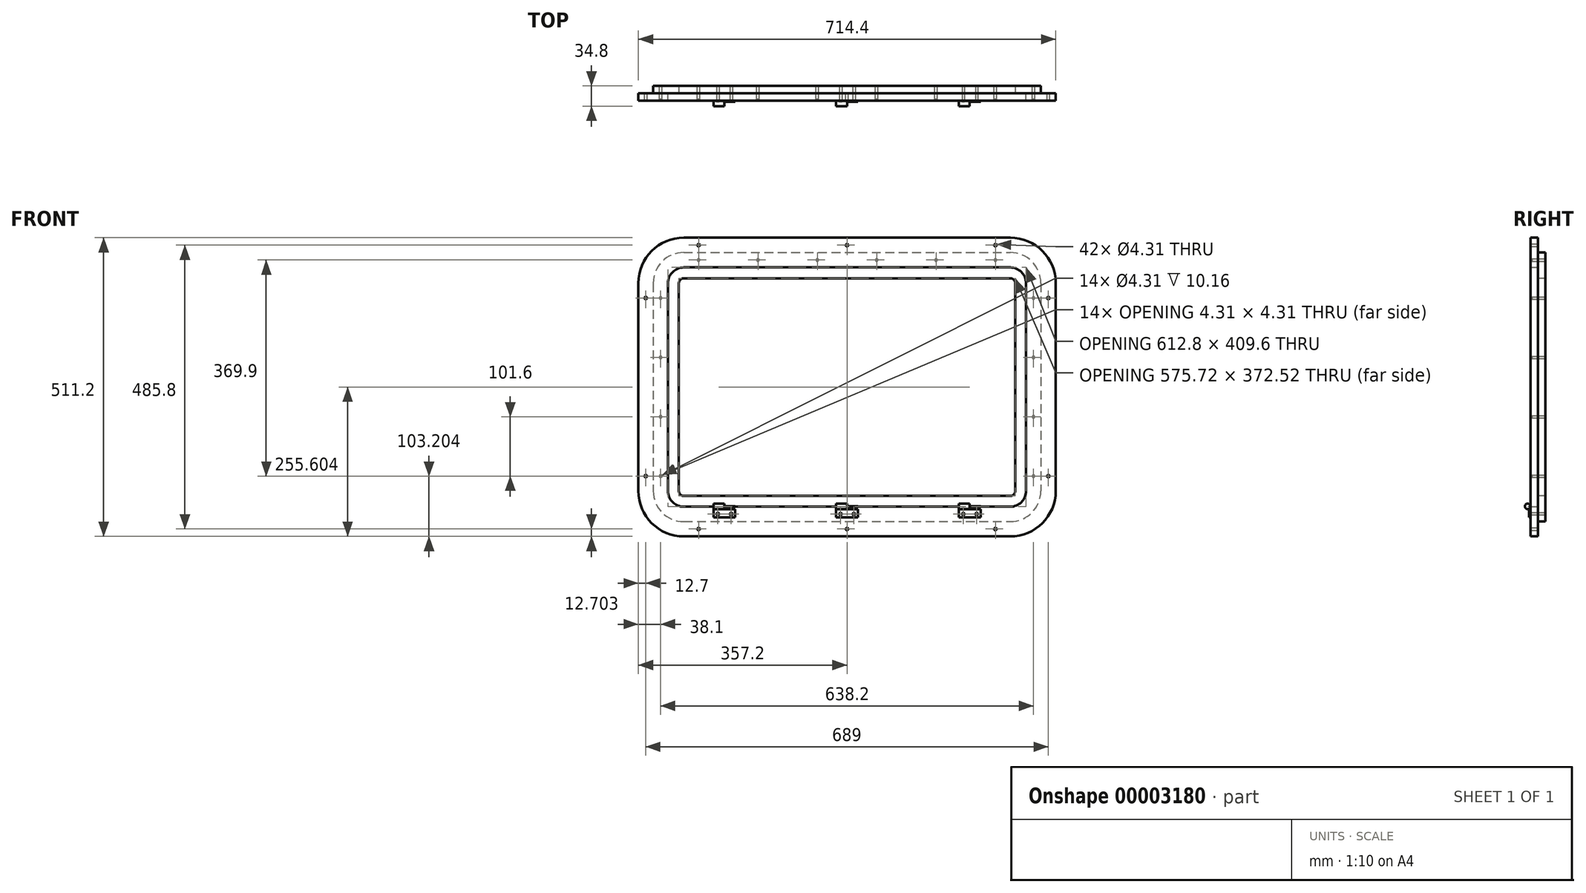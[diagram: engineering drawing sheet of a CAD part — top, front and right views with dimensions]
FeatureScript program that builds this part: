
annotation { "Feature Type Name" : "Feature", "Feature Type Description" : "" }
export const myFeature = defineFeature(function(context is Context, id is Id, definition is map)
    precondition{}
    {
        {
            var Q0;
            Q0=qCreatedBy(makeId("Front.planeOp"),FACE);
            var sketch = newSketch(context, id + "F0", { "sketchPlane" : qUnion([Q0])});
            skLineSegment(sketch, "E0.bottom", {"start": v(-236.07, 236.66) * mm, "end": v(322.73, 236.66) * mm});
            skLineSegment(sketch, "E0.top", {"start": v(-236.07, -169.74) * mm, "end": v(322.73, -169.74) * mm});
            skLineSegment(sketch, "E0.left", {"start": v(-261.47, 211.26) * mm, "end": v(-261.47, -144.34) * mm});
            skLineSegment(sketch, "E0.right", {"start": v(348.13, 211.26) * mm, "end": v(348.13, -144.34) * mm});
            skPoint(sketch, "E1.visualSharp", {"position": v(-261.47, 236.66) * mm});
            skArc(sketch, "E1.filletArc", {"start": v(-236.07, 236.66) * mm, "mid": v(-254.03, 229.22) * mm, "end": v(-261.47, 211.26) * mm});
            skPoint(sketch, "E2.visualSharp", {"position": v(-261.47, -169.74) * mm});
            skArc(sketch, "E2.filletArc", {"start": v(-261.47, -144.34) * mm, "mid": v(-254.03, -162.3) * mm, "end": v(-236.07, -169.74) * mm});
            skPoint(sketch, "E3.visualSharp", {"position": v(348.13, -169.74) * mm});
            skArc(sketch, "E3.filletArc", {"start": v(322.73, -169.74) * mm, "mid": v(340.7, -162.3) * mm, "end": v(348.13, -144.34) * mm});
            skPoint(sketch, "E4.visualSharp", {"position": v(348.13, 236.66) * mm});
            skArc(sketch, "E4.filletArc", {"start": v(348.13, 211.26) * mm, "mid": v(340.7, 229.22) * mm, "end": v(322.73, 236.66) * mm});
            skArc(sketch, "E5.0", {"start": v(-236.07, 238.26) * mm, "mid": v(-255.16, 230.36) * mm, "end": v(-263.07, 211.26) * mm});
            skLineSegment(sketch, "E5.1", {"start": v(-236.07, 238.26) * mm, "end": v(322.73, 238.26) * mm});
            skArc(sketch, "E5.2", {"start": v(349.73, 211.26) * mm, "mid": v(341.82, 230.36) * mm, "end": v(322.73, 238.26) * mm});
            skLineSegment(sketch, "E5.3", {"start": v(349.73, 211.26) * mm, "end": v(349.73, -144.34) * mm});
            skArc(sketch, "E5.4", {"start": v(322.73, -171.34) * mm, "mid": v(341.82, -163.43) * mm, "end": v(349.73, -144.34) * mm});
            skLineSegment(sketch, "E5.5", {"start": v(-263.07, 211.26) * mm, "end": v(-263.07, -144.34) * mm});
            skLineSegment(sketch, "E5.6", {"start": v(-236.07, -171.34) * mm, "end": v(322.73, -171.34) * mm});
            skArc(sketch, "E5.7", {"start": v(-263.07, -144.34) * mm, "mid": v(-255.16, -163.43) * mm, "end": v(-236.07, -171.34) * mm});
            skArc(sketch, "E6.0", {"start": v(-236.07, 219.72) * mm, "mid": v(-242.05, 217.24) * mm, "end": v(-244.53, 211.26) * mm});
            skLineSegment(sketch, "E6.1", {"start": v(-236.07, 219.72) * mm, "end": v(322.73, 219.72) * mm});
            skArc(sketch, "E6.2", {"start": v(331.19, 211.26) * mm, "mid": v(328.71, 217.24) * mm, "end": v(322.73, 219.72) * mm});
            skLineSegment(sketch, "E6.3", {"start": v(331.19, 211.26) * mm, "end": v(331.19, -144.34) * mm});
            skArc(sketch, "E6.4", {"start": v(322.73, -152.8) * mm, "mid": v(328.71, -150.32) * mm, "end": v(331.19, -144.34) * mm});
            skLineSegment(sketch, "E6.5", {"start": v(-244.53, 211.26) * mm, "end": v(-244.53, -144.34) * mm});
            skLineSegment(sketch, "E6.6", {"start": v(-236.07, -152.8) * mm, "end": v(322.73, -152.8) * mm});
            skArc(sketch, "E6.7", {"start": v(-244.53, -144.34) * mm, "mid": v(-242.05, -150.32) * mm, "end": v(-236.07, -152.8) * mm});
            skArc(sketch, "E7.0", {"start": v(-236.07, 289.06) * mm, "mid": v(-291.08, 266.28) * mm, "end": v(-313.87, 211.26) * mm});
            skLineSegment(sketch, "E7.1", {"start": v(-236.07, 289.06) * mm, "end": v(322.73, 289.06) * mm});
            skArc(sketch, "E7.2", {"start": v(400.53, 211.26) * mm, "mid": v(377.74, 266.28) * mm, "end": v(322.73, 289.06) * mm});
            skLineSegment(sketch, "E7.3", {"start": v(400.53, 211.26) * mm, "end": v(400.53, -144.34) * mm});
            skArc(sketch, "E7.4", {"start": v(322.73, -222.14) * mm, "mid": v(377.74, -199.35) * mm, "end": v(400.53, -144.34) * mm});
            skLineSegment(sketch, "E7.5", {"start": v(-313.87, 211.26) * mm, "end": v(-313.87, -144.34) * mm});
            skLineSegment(sketch, "E7.6", {"start": v(-236.07, -222.14) * mm, "end": v(322.73, -222.14) * mm});
            skArc(sketch, "E7.7", {"start": v(-313.87, -144.34) * mm, "mid": v(-291.08, -199.35) * mm, "end": v(-236.07, -222.14) * mm});
            skArc(sketch, "E8.0", {"start": v(-236.07, 263.66) * mm, "mid": v(-273.12, 248.32) * mm, "end": v(-288.47, 211.26) * mm});
            skLineSegment(sketch, "E8.1", {"start": v(-236.07, 263.66) * mm, "end": v(322.73, 263.66) * mm});
            skArc(sketch, "E8.2", {"start": v(375.13, 211.26) * mm, "mid": v(359.78, 248.32) * mm, "end": v(322.73, 263.66) * mm});
            skLineSegment(sketch, "E8.3", {"start": v(375.13, 211.26) * mm, "end": v(375.13, -144.34) * mm});
            skArc(sketch, "E8.4", {"start": v(322.73, -196.74) * mm, "mid": v(359.78, -181.39) * mm, "end": v(375.13, -144.34) * mm});
            skLineSegment(sketch, "E8.5", {"start": v(-288.47, 211.26) * mm, "end": v(-288.47, -144.34) * mm});
            skLineSegment(sketch, "E8.6", {"start": v(-236.07, -196.74) * mm, "end": v(322.73, -196.74) * mm});
            skArc(sketch, "E8.7", {"start": v(-288.47, -144.34) * mm, "mid": v(-273.12, -181.39) * mm, "end": v(-236.07, -196.74) * mm});
            skSolve(sketch);
        }
        {
            var Q0;
            Q0=makeQuery(id+"F0.imprint","IMPRINT",FACE,{"disambiguationData":[TD([[makeQuery(id+"F0.imprint","IMPRINT",EDGE,{"derivedFrom":sQuery(id+"F0.wireOp",EDGE,"E5.0")}),-1.0]])]});
            var Q1;
            Q1=makeQuery(id+"F0.imprint","IMPRINT",FACE,{"disambiguationData":[TD([[makeQuery(id+"F0.imprint","IMPRINT",EDGE,{"derivedFrom":sQuery(id+"F0.wireOp",EDGE,"E0.bottom")}),1.0]])]});
            var Q2;
            Q2=makeQuery(id+"F0.imprint","IMPRINT",FACE,{"disambiguationData":[TD([[makeQuery(id+"F0.imprint","IMPRINT",EDGE,{"derivedFrom":sQuery(id+"F0.wireOp",EDGE,"E0.bottom")}),-1.0]])]});
            extrude(context, id + "F1", {"entities" : qUnion([Q0, Q1, Q2]), "oppositeDirection" : true, "depth" : 12.7 * mm});
        }
        {
            var Q0;
            Q0=makeQuery(id+"F0.imprint","IMPRINT",FACE,{"disambiguationData":[TD([[makeQuery(id+"F0.imprint","IMPRINT",EDGE,{"derivedFrom":sQuery(id+"F0.wireOp",EDGE,"E7.0")}),1.0]])]});
            var Q1;
            Q1=makeQuery(id+"F0.imprint","IMPRINT",FACE,{"disambiguationData":[TD([[makeQuery(id+"F0.imprint","IMPRINT",EDGE,{"derivedFrom":sQuery(id+"F0.wireOp",EDGE,"E5.0")}),-1.0]])]});
            extrude(context, id + "F2", {"entities" : qUnion([Q0, Q1]), "depth" : 12.7 * mm});
        }
        {
            var Q0;
            Q0=makeQuery(id+"F2.opExtrude","CAP_FACE",FACE,{"disambiguationData":[OSD([sQuery(id+"F0.wireOp",EDGE,"E5.0"),sQuery(id+"F0.wireOp",EDGE,"E5.1"),sQuery(id+"F0.wireOp",EDGE,"E5.2"),sQuery(id+"F0.wireOp",EDGE,"E5.3"),sQuery(id+"F0.wireOp",EDGE,"E5.4"),sQuery(id+"F0.wireOp",EDGE,"E5.5"),sQuery(id+"F0.wireOp",EDGE,"E5.6"),sQuery(id+"F0.wireOp",EDGE,"E5.7"),sQuery(id+"F0.wireOp",EDGE,"E7.0"),sQuery(id+"F0.wireOp",EDGE,"E7.1"),sQuery(id+"F0.wireOp",EDGE,"E7.2"),sQuery(id+"F0.wireOp",EDGE,"E7.3"),sQuery(id+"F0.wireOp",EDGE,"E7.4"),sQuery(id+"F0.wireOp",EDGE,"E7.5"),sQuery(id+"F0.wireOp",EDGE,"E7.6"),sQuery(id+"F0.wireOp",EDGE,"E7.7")])],"isStart":false});
            var sketch = newSketch(context, id + "F3", { "sketchPlane" : qUnion([Q0])});
            skLineSegment(sketch, "E9.0", {"start": v(-261.47, 211.26) * mm, "end": v(-261.47, -144.34) * mm});
            skLineSegment(sketch, "E9.1", {"start": v(-236.07, -169.74) * mm, "end": v(322.73, -169.74) * mm});
            skLineSegment(sketch, "E10.bottom", {"start": v(-185.27, -189.6) * mm, "end": v(-148.19, -189.6) * mm});
            skLineSegment(sketch, "E10.top", {"start": v(-185.27, -170.55) * mm, "end": v(-148.19, -170.55) * mm});
            skLineSegment(sketch, "E10.left", {"start": v(-185.27, -189.6) * mm, "end": v(-185.27, -170.55) * mm});
            skLineSegment(sketch, "E10.right", {"start": v(-148.19, -189.6) * mm, "end": v(-148.19, -170.55) * mm});
            skLineSegment(sketch, "E11.bottom", {"start": v(-166.85, -170.55) * mm, "end": v(-148.19, -170.55) * mm});
            skLineSegment(sketch, "E11.top", {"start": v(-166.85, -175.32) * mm, "end": v(-148.19, -175.32) * mm});
            skLineSegment(sketch, "E11.left", {"start": v(-166.85, -170.55) * mm, "end": v(-166.85, -175.32) * mm});
            skLineSegment(sketch, "E11.right", {"start": v(-148.19, -170.55) * mm, "end": v(-148.19, -175.32) * mm});
            skCircle(sketch, "E12", {"center": v(-177.78, -183.76) * mm, "radius": 2.15 * mm});
            skCircle(sketch, "E13", {"center": v(-154.92, -183.76) * mm, "radius": 2.15 * mm});
            skSolve(sketch);
        }
        {
            var Q0;
            {var subQ6=sQuery(id+"F3.wireOp",EDGE,"E10.bottom");Q0=makeQuery(id+"F3.imprint","IMPRINT",FACE,{"disambiguationData":[TD([[makeQuery(id+"F3.imprint","IMPRINT",EDGE,{"derivedFrom":subQ6}),1.0]])]});}
            var Q1;
            {var subQ5=sQuery(id+"F3.wireOp",EDGE,"E10.top");Q1=makeQuery(id+"F3.imprint","IMPRINT",FACE,{"disambiguationData":[TD([[makeQuery(id+"F3.imprint","IMPRINT",EDGE,{"derivedFrom":subQ5}),-1.0]])]});}
            var Q2;
            {var subQ3=sQuery(id+"F3.wireOp",EDGE,"E10.left");var subQ5=sQuery(id+"F3.wireOp",EDGE,"E9.1");var subQ7=makeQuery(id+"F3.imprint","INTERSECT",VERTEX,{"derivedFrom":[subQ5,subQ3]});Q2=makeQuery(id+"F3.imprint","IMPRINT",FACE,{"disambiguationData":[TD([[makeQuery(id+"F3.imprint","IMPRINT",EDGE,{"disambiguationData":[TD([[subQ7,-1.0]])],"derivedFrom":subQ5}),-1.0]])]});}
            extrude(context, id + "F4", {"entities" : qUnion([Q0, Q1, Q2]), "depth" : 2.03 * mm});
        }
        {
            var Q0;
            Q0=makeQuery(id+"F4.opExtrude","SWEPT_FACE",FACE,{"disambiguationData":[OSD([sQuery(id+"F3.wireOp",EDGE,"E10.left")])]});
            var sketch = newSketch(context, id + "F5", { "sketchPlane" : qUnion([Q0])});
            skCircle(sketch, "E14", {"center": v(17.4, -170.55) * mm, "radius": 4.7 * mm});
            skSolve(sketch);
        }
        {
            var Q0;
            {var subQ0=sQuery(id+"F3.wireOp",EDGE,"E10.left");var subQ4=makeQuery(id+"F4.opExtrude","SWEPT_EDGE",EDGE,{"disambiguationData":[OSD([sQuery(id+"F3.wireOp",EDGE,"E10.top"),subQ0])]});Q0=makeQuery(id+"F5.imprint","IMPRINT",FACE,{"disambiguationData":[TD([[makeQuery(id+"F5.imprint","IMPRINT",EDGE,{"derivedFrom":subQ4}),-1.0]])]});}
            var Q1;
            {var subQ0=sQuery(id+"F3.wireOp",EDGE,"E10.left");var subQ4=makeQuery(id+"F4.opExtrude","SWEPT_EDGE",EDGE,{"disambiguationData":[OSD([sQuery(id+"F3.wireOp",EDGE,"E10.top"),subQ0])]});Q1=makeQuery(id+"F5.imprint","IMPRINT",FACE,{"disambiguationData":[TD([[makeQuery(id+"F5.imprint","IMPRINT",EDGE,{"derivedFrom":subQ4}),1.0]])]});}
            extrude(context, id + "F6", {"entities" : qUnion([Q0, Q1]), "operationType" : NewBodyOperationType.ADD, "oppositeDirection" : true, "depth" : 18.54 * mm});
        }
        {
            var Q0;
            Q0=makeQuery(id+"F4.opExtrude","SWEPT_BODY",BODY,{"disambiguationData":[OSD([sQuery(id+"F3.wireOp",EDGE,"E10.bottom"),sQuery(id+"F3.wireOp",EDGE,"E10.top"),sQuery(id+"F3.wireOp",EDGE,"E10.left"),sQuery(id+"F3.wireOp",EDGE,"E10.right"),sQuery(id+"F3.wireOp",EDGE,"E11.top"),sQuery(id+"F3.wireOp",EDGE,"E11.left"),sQuery(id+"F3.wireOp",EDGE,"E12"),sQuery(id+"F3.wireOp",EDGE,"E13")])]});
            var Q1;
            Q1=sQuery(id+"F3.wireOp",EDGE,"E9.0");
            var Q2;
            Q2=sQuery(id+"F3.wireOp",EDGE,"E9.1");
            transform(context, id + "F7", {"entities" : qUnion([Q0]), "transformType" : TransformType.TRANSLATION_3D, "dx" : 210.06 * mm, "dy" : 0 * mm, "dz" : 0 * mm, "makeCopy" : true});
        }
        {
            var Q0;
            Q0=makeQuery(id+"F4.opExtrude","SWEPT_BODY",BODY,{"disambiguationData":[OSD([sQuery(id+"F3.wireOp",EDGE,"E10.bottom"),sQuery(id+"F3.wireOp",EDGE,"E10.top"),sQuery(id+"F3.wireOp",EDGE,"E10.left"),sQuery(id+"F3.wireOp",EDGE,"E10.right"),sQuery(id+"F3.wireOp",EDGE,"E11.top"),sQuery(id+"F3.wireOp",EDGE,"E11.left"),sQuery(id+"F3.wireOp",EDGE,"E12"),sQuery(id+"F3.wireOp",EDGE,"E13")])]});
            var Q1;
            Q1=sQuery(id+"F3.wireOp",EDGE,"E9.1");
            transform(context, id + "F8", {"entities" : qUnion([Q0]), "transformType" : TransformType.TRANSLATION_3D, "dx" : 420.12 * mm, "dy" : 0 * mm, "dz" : 0 * mm, "makeCopy" : true});
        }
        {
            var Q0;
            {var subQ8=sQuery(id+"F3.wireOp",EDGE,"E10.bottom");Q0=makeQuery(id+"F3.imprint","IMPRINT",FACE,{"disambiguationData":[TD([[makeQuery(id+"F3.imprint","IMPRINT",EDGE,{"derivedFrom":subQ8}),-1.0]])]});}
            var sketch = newSketch(context, id + "F9", { "sketchPlane" : qUnion([Q0])});
            skCircle(sketch, "E15.0", {"center": v(-177.78, -183.76) * mm, "radius": 2.15 * mm});
            skCircle(sketch, "E15.1", {"center": v(-154.92, -183.76) * mm, "radius": 2.15 * mm});
            skCircle(sketch, "E15.2", {"center": v(32.28, -183.76) * mm, "radius": 2.15 * mm});
            skCircle(sketch, "E15.3", {"center": v(55.14, -183.76) * mm, "radius": 2.15 * mm});
            skCircle(sketch, "E15.4", {"center": v(242.34, -183.76) * mm, "radius": 2.15 * mm});
            skCircle(sketch, "E15.5", {"center": v(265.2, -183.76) * mm, "radius": 2.15 * mm});
            skSolve(sketch);
        }
        {
            var Q0;
            Q0=makeQuery(id+"F9.imprint","IMPRINT",FACE,{"disambiguationData":[TD([[makeQuery(id+"F9.imprint","IMPRINT",EDGE,{"derivedFrom":sQuery(id+"F9.wireOp",EDGE,"E15.0")}),1.0]])]});
            var Q1;
            Q1=makeQuery(id+"F9.imprint","IMPRINT",FACE,{"disambiguationData":[TD([[makeQuery(id+"F9.imprint","IMPRINT",EDGE,{"derivedFrom":sQuery(id+"F9.wireOp",EDGE,"E15.1")}),1.0]])]});
            var Q2;
            Q2=makeQuery(id+"F9.imprint","IMPRINT",FACE,{"disambiguationData":[TD([[makeQuery(id+"F9.imprint","IMPRINT",EDGE,{"derivedFrom":sQuery(id+"F9.wireOp",EDGE,"E15.2")}),1.0]])]});
            var Q3;
            Q3=makeQuery(id+"F9.imprint","IMPRINT",FACE,{"disambiguationData":[TD([[makeQuery(id+"F9.imprint","IMPRINT",EDGE,{"derivedFrom":sQuery(id+"F9.wireOp",EDGE,"E15.3")}),1.0]])]});
            var Q4;
            Q4=makeQuery(id+"F9.imprint","IMPRINT",FACE,{"disambiguationData":[TD([[makeQuery(id+"F9.imprint","IMPRINT",EDGE,{"derivedFrom":sQuery(id+"F9.wireOp",EDGE,"E15.4")}),1.0]])]});
            var Q5;
            Q5=makeQuery(id+"F9.imprint","IMPRINT",FACE,{"disambiguationData":[TD([[makeQuery(id+"F9.imprint","IMPRINT",EDGE,{"derivedFrom":sQuery(id+"F9.wireOp",EDGE,"E15.5")}),1.0]])]});
            extrude(context, id + "F10", {"entities" : qUnion([Q0, Q1, Q2, Q3, Q4, Q5]), "operationType" : NewBodyOperationType.REMOVE, "oppositeDirection" : true, "depth" : 25.4 * mm});
        }
        {
            var Q0;
            Q0=makeQuery(id+"F1.opExtrude","CAP_FACE",FACE,{"disambiguationData":[OSD([sQuery(id+"F0.wireOp",EDGE,"E6.0"),sQuery(id+"F0.wireOp",EDGE,"E6.1"),sQuery(id+"F0.wireOp",EDGE,"E6.2"),sQuery(id+"F0.wireOp",EDGE,"E6.3"),sQuery(id+"F0.wireOp",EDGE,"E6.4"),sQuery(id+"F0.wireOp",EDGE,"E6.5"),sQuery(id+"F0.wireOp",EDGE,"E6.6"),sQuery(id+"F0.wireOp",EDGE,"E6.7"),sQuery(id+"F0.wireOp",EDGE,"E8.0"),sQuery(id+"F0.wireOp",EDGE,"E8.1"),sQuery(id+"F0.wireOp",EDGE,"E8.2"),sQuery(id+"F0.wireOp",EDGE,"E8.3"),sQuery(id+"F0.wireOp",EDGE,"E8.4"),sQuery(id+"F0.wireOp",EDGE,"E8.5"),sQuery(id+"F0.wireOp",EDGE,"E8.6"),sQuery(id+"F0.wireOp",EDGE,"E8.7")])],"isStart":false});
            var sketch = newSketch(context, id + "F11", { "sketchPlane" : qUnion([Q0])});
            skCircle(sketch, "E16", {"center": v(-297.33, 250.96) * mm, "radius": 2.15 * mm});
            skCircle(sketch, "E17.1.0.0", {"center": v(-195.73, 250.96) * mm, "radius": 2.15 * mm});
            skCircle(sketch, "E17.2.0.0", {"center": v(-94.13, 250.96) * mm, "radius": 2.15 * mm});
            skLineSegment(sketch, "E17.direction1", {"start": v(-297.33, 250.96) * mm, "end": v(-195.73, 250.96) * mm, "construction": true});
            skCircle(sketch, "E18.0.3.0", {"center": v(7.47, 250.96) * mm, "radius": 2.15 * mm});
            skCircle(sketch, "E18.0.4.0", {"center": v(109.07, 250.96) * mm, "radius": 2.15 * mm});
            skCircle(sketch, "E19.0.5.0", {"center": v(210.67, 250.96) * mm, "radius": 2.15 * mm});
            skCircle(sketch, "E20", {"center": v(-362.43, 185.86) * mm, "radius": 2.15 * mm});
            skCircle(sketch, "E21.0.1.0", {"center": v(-362.43, 84.26) * mm, "radius": 2.15 * mm});
            skCircle(sketch, "E21.0.2.0", {"center": v(-362.43, -17.34) * mm, "radius": 2.15 * mm});
            skCircle(sketch, "E21.0.3.0", {"center": v(-362.43, -118.94) * mm, "radius": 2.15 * mm});
            skLineSegment(sketch, "E21.direction1", {"start": v(-362.43, 185.86) * mm, "end": v(-337.03, 185.86) * mm, "construction": true});
            skLineSegment(sketch, "E21.direction2", {"start": v(-362.43, 185.86) * mm, "end": v(-362.43, 84.26) * mm, "construction": true});
            skLineSegment(sketch, "E22.0", {"start": v(288.47, 211.26) * mm, "end": v(288.47, -144.34) * mm});
            skCircle(sketch, "E23", {"center": v(275.77, 185.86) * mm, "radius": 2.15 * mm});
            skCircle(sketch, "E24.0.1.0", {"center": v(275.77, 84.26) * mm, "radius": 2.15 * mm});
            skCircle(sketch, "E24.0.2.0", {"center": v(275.77, -17.34) * mm, "radius": 2.15 * mm});
            skCircle(sketch, "E24.0.3.0", {"center": v(275.77, -118.94) * mm, "radius": 2.15 * mm});
            skLineSegment(sketch, "E24.direction1", {"start": v(275.77, 185.86) * mm, "end": v(301.17, 185.86) * mm, "construction": true});
            skLineSegment(sketch, "E24.direction2", {"start": v(275.77, 185.86) * mm, "end": v(275.77, 84.26) * mm, "construction": true});
            skSolve(sketch);
        }
        {
            var Q0;
            Q0=makeQuery(id+"F11.imprint","IMPRINT",FACE,{"disambiguationData":[TD([[makeQuery(id+"F11.imprint","IMPRINT",EDGE,{"derivedFrom":sQuery(id+"F11.wireOp",EDGE,"E21.0.3.0")}),1.0]])]});
            var Q1;
            Q1=makeQuery(id+"F11.imprint","IMPRINT",FACE,{"disambiguationData":[TD([[makeQuery(id+"F11.imprint","IMPRINT",EDGE,{"derivedFrom":sQuery(id+"F11.wireOp",EDGE,"E21.0.2.0")}),1.0]])]});
            var Q2;
            Q2=makeQuery(id+"F11.imprint","IMPRINT",FACE,{"disambiguationData":[TD([[makeQuery(id+"F11.imprint","IMPRINT",EDGE,{"derivedFrom":sQuery(id+"F11.wireOp",EDGE,"E21.0.1.0")}),1.0]])]});
            var Q3;
            Q3=makeQuery(id+"F11.imprint","IMPRINT",FACE,{"disambiguationData":[TD([[makeQuery(id+"F11.imprint","IMPRINT",EDGE,{"derivedFrom":sQuery(id+"F11.wireOp",EDGE,"E20")}),1.0]])]});
            var Q4;
            Q4=makeQuery(id+"F11.imprint","IMPRINT",FACE,{"disambiguationData":[TD([[makeQuery(id+"F11.imprint","IMPRINT",EDGE,{"derivedFrom":sQuery(id+"F11.wireOp",EDGE,"E16")}),1.0]])]});
            var Q5;
            Q5=makeQuery(id+"F11.imprint","IMPRINT",FACE,{"disambiguationData":[TD([[makeQuery(id+"F11.imprint","IMPRINT",EDGE,{"derivedFrom":sQuery(id+"F11.wireOp",EDGE,"E17.1.0.0")}),1.0]])]});
            var Q6;
            Q6=makeQuery(id+"F11.imprint","IMPRINT",FACE,{"disambiguationData":[TD([[makeQuery(id+"F11.imprint","IMPRINT",EDGE,{"derivedFrom":sQuery(id+"F11.wireOp",EDGE,"E17.2.0.0")}),1.0]])]});
            var Q7;
            Q7=makeQuery(id+"F11.imprint","IMPRINT",FACE,{"disambiguationData":[TD([[makeQuery(id+"F11.imprint","IMPRINT",EDGE,{"derivedFrom":sQuery(id+"F11.wireOp",EDGE,"E18.0.3.0")}),1.0]])]});
            var Q8;
            Q8=makeQuery(id+"F11.imprint","IMPRINT",FACE,{"disambiguationData":[TD([[makeQuery(id+"F11.imprint","IMPRINT",EDGE,{"derivedFrom":sQuery(id+"F11.wireOp",EDGE,"E18.0.4.0")}),1.0]])]});
            var Q9;
            Q9=makeQuery(id+"F11.imprint","IMPRINT",FACE,{"disambiguationData":[TD([[makeQuery(id+"F11.imprint","IMPRINT",EDGE,{"derivedFrom":sQuery(id+"F11.wireOp",EDGE,"E19.0.5.0")}),1.0]])]});
            var Q10;
            Q10=makeQuery(id+"F11.imprint","IMPRINT",FACE,{"disambiguationData":[TD([[makeQuery(id+"F11.imprint","IMPRINT",EDGE,{"derivedFrom":sQuery(id+"F11.wireOp",EDGE,"E23")}),1.0]])]});
            var Q11;
            Q11=makeQuery(id+"F11.imprint","IMPRINT",FACE,{"disambiguationData":[TD([[makeQuery(id+"F11.imprint","IMPRINT",EDGE,{"derivedFrom":sQuery(id+"F11.wireOp",EDGE,"E24.0.1.0")}),1.0]])]});
            var Q12;
            Q12=makeQuery(id+"F11.imprint","IMPRINT",FACE,{"disambiguationData":[TD([[makeQuery(id+"F11.imprint","IMPRINT",EDGE,{"derivedFrom":sQuery(id+"F11.wireOp",EDGE,"E24.0.2.0")}),1.0]])]});
            var Q13;
            Q13=makeQuery(id+"F11.imprint","IMPRINT",FACE,{"disambiguationData":[TD([[makeQuery(id+"F11.imprint","IMPRINT",EDGE,{"derivedFrom":sQuery(id+"F11.wireOp",EDGE,"E24.0.3.0")}),1.0]])]});
            extrude(context, id + "F12", {"entities" : qUnion([Q0, Q1, Q2, Q3, Q4, Q5, Q6, Q7, Q8, Q9, Q10, Q11, Q12, Q13]), "operationType" : NewBodyOperationType.REMOVE, "oppositeDirection" : true, "depth" : 22.86 * mm});
        }
        {
            var Q0;
            Q0=makeQuery(id+"F0.imprint","IMPRINT",FACE,{"disambiguationData":[TD([[makeQuery(id+"F0.imprint","IMPRINT",EDGE,{"derivedFrom":sQuery(id+"F0.wireOp",EDGE,"E7.0")}),1.0]])]});
            var sketch = newSketch(context, id + "F13", { "sketchPlane" : qUnion([Q0])});
            skCircle(sketch, "E25", {"center": v(362.43, 185.86) * mm, "radius": 1.38 * mm});
            skCircle(sketch, "E26", {"center": v(297.33, 250.96) * mm, "radius": 1.38 * mm});
            skCircle(sketch, "E27", {"center": v(195.73, 250.96) * mm, "radius": 1.38 * mm});
            skCircle(sketch, "E28", {"center": v(94.13, 250.96) * mm, "radius": 1.38 * mm});
            skCircle(sketch, "E29", {"center": v(-7.47, 250.96) * mm, "radius": 1.38 * mm});
            skCircle(sketch, "E30", {"center": v(362.43, 84.26) * mm, "radius": 1.38 * mm});
            skCircle(sketch, "E31", {"center": v(362.43, -17.34) * mm, "radius": 1.38 * mm});
            skCircle(sketch, "E32", {"center": v(362.43, -118.94) * mm, "radius": 1.38 * mm});
            skCircle(sketch, "E33", {"center": v(-109.07, 250.96) * mm, "radius": 1.38 * mm});
            skCircle(sketch, "E34", {"center": v(-210.67, 250.96) * mm, "radius": 1.38 * mm});
            skCircle(sketch, "E35", {"center": v(-275.77, 185.86) * mm, "radius": 1.38 * mm});
            skCircle(sketch, "E36", {"center": v(-275.77, 84.26) * mm, "radius": 1.38 * mm});
            skCircle(sketch, "E37", {"center": v(-275.77, -17.34) * mm, "radius": 1.38 * mm});
            skCircle(sketch, "E38", {"center": v(-275.77, -118.94) * mm, "radius": 1.38 * mm});
            skSolve(sketch);
        }
        {
            var Q0;
            Q0=makeQuery(id+"F13.imprint","IMPRINT",FACE,{"disambiguationData":[TD([[makeQuery(id+"F13.imprint","IMPRINT",EDGE,{"derivedFrom":sQuery(id+"F13.wireOp",EDGE,"E29")}),1.0]])]});
            var Q1;
            Q1=makeQuery(id+"F13.imprint","IMPRINT",FACE,{"disambiguationData":[TD([[makeQuery(id+"F13.imprint","IMPRINT",EDGE,{"derivedFrom":sQuery(id+"F13.wireOp",EDGE,"E36")}),1.0]])]});
            var Q2;
            Q2=makeQuery(id+"F13.imprint","IMPRINT",FACE,{"disambiguationData":[TD([[makeQuery(id+"F13.imprint","IMPRINT",EDGE,{"derivedFrom":sQuery(id+"F13.wireOp",EDGE,"E32")}),1.0]])]});
            var Q3;
            Q3=makeQuery(id+"F13.imprint","IMPRINT",FACE,{"disambiguationData":[TD([[makeQuery(id+"F13.imprint","IMPRINT",EDGE,{"derivedFrom":sQuery(id+"F13.wireOp",EDGE,"E33")}),1.0]])]});
            var Q4;
            Q4=makeQuery(id+"F13.imprint","IMPRINT",FACE,{"disambiguationData":[TD([[makeQuery(id+"F13.imprint","IMPRINT",EDGE,{"derivedFrom":sQuery(id+"F13.wireOp",EDGE,"E37")}),1.0]])]});
            var Q5;
            Q5=makeQuery(id+"F13.imprint","IMPRINT",FACE,{"disambiguationData":[TD([[makeQuery(id+"F13.imprint","IMPRINT",EDGE,{"derivedFrom":sQuery(id+"F13.wireOp",EDGE,"E26")}),1.0]])]});
            var Q6;
            Q6=makeQuery(id+"F13.imprint","IMPRINT",FACE,{"disambiguationData":[TD([[makeQuery(id+"F13.imprint","IMPRINT",EDGE,{"derivedFrom":sQuery(id+"F13.wireOp",EDGE,"E25")}),1.0]])]});
            var Q7;
            Q7=makeQuery(id+"F13.imprint","IMPRINT",FACE,{"disambiguationData":[TD([[makeQuery(id+"F13.imprint","IMPRINT",EDGE,{"derivedFrom":sQuery(id+"F13.wireOp",EDGE,"E35")}),1.0]])]});
            var Q8;
            Q8=makeQuery(id+"F13.imprint","IMPRINT",FACE,{"disambiguationData":[TD([[makeQuery(id+"F13.imprint","IMPRINT",EDGE,{"derivedFrom":sQuery(id+"F13.wireOp",EDGE,"E31")}),1.0]])]});
            var Q9;
            Q9=makeQuery(id+"F13.imprint","IMPRINT",FACE,{"disambiguationData":[TD([[makeQuery(id+"F13.imprint","IMPRINT",EDGE,{"derivedFrom":sQuery(id+"F13.wireOp",EDGE,"E28")}),1.0]])]});
            var Q10;
            Q10=makeQuery(id+"F13.imprint","IMPRINT",FACE,{"disambiguationData":[TD([[makeQuery(id+"F13.imprint","IMPRINT",EDGE,{"derivedFrom":sQuery(id+"F13.wireOp",EDGE,"E30")}),1.0]])]});
            var Q11;
            Q11=makeQuery(id+"F13.imprint","IMPRINT",FACE,{"disambiguationData":[TD([[makeQuery(id+"F13.imprint","IMPRINT",EDGE,{"derivedFrom":sQuery(id+"F13.wireOp",EDGE,"E27")}),1.0]])]});
            var Q12;
            Q12=makeQuery(id+"F13.imprint","IMPRINT",FACE,{"disambiguationData":[TD([[makeQuery(id+"F13.imprint","IMPRINT",EDGE,{"derivedFrom":sQuery(id+"F13.wireOp",EDGE,"E34")}),1.0]])]});
            var Q13;
            Q13=makeQuery(id+"F13.imprint","IMPRINT",FACE,{"disambiguationData":[TD([[makeQuery(id+"F13.imprint","IMPRINT",EDGE,{"derivedFrom":sQuery(id+"F13.wireOp",EDGE,"E38")}),1.0]])]});
            var Q14;
            Q14=sQuery(id+"F13.wireOp",EDGE,"E37");
            var Q15;
            Q15=sQuery(id+"F13.wireOp",EDGE,"E31");
            var Q16;
            Q16=sQuery(id+"F13.wireOp",EDGE,"E28");
            var Q17;
            Q17=sQuery(id+"F13.wireOp",EDGE,"E36");
            var Q18;
            Q18=sQuery(id+"F13.wireOp",EDGE,"E29");
            var Q19;
            Q19=sQuery(id+"F13.wireOp",EDGE,"E34");
            var Q20;
            Q20=sQuery(id+"F13.wireOp",EDGE,"E35");
            var Q21;
            Q21=sQuery(id+"F13.wireOp",EDGE,"E32");
            var Q22;
            Q22=sQuery(id+"F13.wireOp",EDGE,"E38");
            var Q23;
            Q23=sQuery(id+"F13.wireOp",EDGE,"E30");
            var Q24;
            Q24=sQuery(id+"F13.wireOp",EDGE,"E26");
            var Q25;
            Q25=sQuery(id+"F13.wireOp",EDGE,"E27");
            var Q26;
            Q26=sQuery(id+"F13.wireOp",EDGE,"E33");
            var Q27;
            Q27=sQuery(id+"F13.wireOp",EDGE,"E25");
            extrude(context, id + "F14", {"entities" : qUnion([Q0, Q1, Q2, Q3, Q4, Q5, Q6, Q7, Q8, Q9, Q10, Q11, Q12, Q13]), "operationType" : NewBodyOperationType.REMOVE, "surfaceEntities" : qUnion([Q14, Q15, Q16, Q17, Q18, Q19, Q20, Q21, Q22, Q23, Q24, Q25, Q26, Q27]), "depth" : 10.16 * mm});
        }
        {
            var Q0;
            Q0=makeQuery(id+"F2.opExtrude","CAP_FACE",FACE,{"disambiguationData":[OSD([sQuery(id+"F0.wireOp",EDGE,"E5.0"),sQuery(id+"F0.wireOp",EDGE,"E5.1"),sQuery(id+"F0.wireOp",EDGE,"E5.2"),sQuery(id+"F0.wireOp",EDGE,"E5.3"),sQuery(id+"F0.wireOp",EDGE,"E5.4"),sQuery(id+"F0.wireOp",EDGE,"E5.5"),sQuery(id+"F0.wireOp",EDGE,"E5.6"),sQuery(id+"F0.wireOp",EDGE,"E5.7"),sQuery(id+"F0.wireOp",EDGE,"E7.0"),sQuery(id+"F0.wireOp",EDGE,"E7.1"),sQuery(id+"F0.wireOp",EDGE,"E7.2"),sQuery(id+"F0.wireOp",EDGE,"E7.3"),sQuery(id+"F0.wireOp",EDGE,"E7.4"),sQuery(id+"F0.wireOp",EDGE,"E7.5"),sQuery(id+"F0.wireOp",EDGE,"E7.6"),sQuery(id+"F0.wireOp",EDGE,"E7.7")])],"isStart":true});
            var sketch = newSketch(context, id + "F15", { "sketchPlane" : qUnion([Q0])});
            skCircle(sketch, "E39", {"center": v(-297.33, 276.36) * mm, "radius": 2.15 * mm});
            skCircle(sketch, "E40", {"center": v(-387.83, 185.86) * mm, "radius": 2.15 * mm});
            skCircle(sketch, "E41", {"center": v(301.17, 185.86) * mm, "radius": 2.15 * mm});
            skCircle(sketch, "E42", {"center": v(-297.33, -209.44) * mm, "radius": 2.15 * mm});
            skCircle(sketch, "E43", {"center": v(-387.83, -118.94) * mm, "radius": 2.15 * mm});
            skCircle(sketch, "E44", {"center": v(-43.33, 276.36) * mm, "radius": 2.15 * mm});
            skCircle(sketch, "E45", {"center": v(210.67, 276.36) * mm, "radius": 2.15 * mm});
            skCircle(sketch, "E46", {"center": v(301.17, -118.94) * mm, "radius": 2.15 * mm});
            skCircle(sketch, "E47", {"center": v(-43.33, -209.44) * mm, "radius": 2.15 * mm});
            skCircle(sketch, "E48", {"center": v(210.67, -209.44) * mm, "radius": 2.15 * mm});
            skSolve(sketch);
        }
        {
            var Q0;
            Q0=makeQuery(id+"F15.imprint","IMPRINT",FACE,{"disambiguationData":[TD([[makeQuery(id+"F15.imprint","IMPRINT",EDGE,{"derivedFrom":sQuery(id+"F15.wireOp",EDGE,"E43")}),1.0]])]});
            var Q1;
            Q1=makeQuery(id+"F15.imprint","IMPRINT",FACE,{"disambiguationData":[TD([[makeQuery(id+"F15.imprint","IMPRINT",EDGE,{"derivedFrom":sQuery(id+"F15.wireOp",EDGE,"E40")}),1.0]])]});
            var Q2;
            Q2=makeQuery(id+"F15.imprint","IMPRINT",FACE,{"disambiguationData":[TD([[makeQuery(id+"F15.imprint","IMPRINT",EDGE,{"derivedFrom":sQuery(id+"F15.wireOp",EDGE,"E44")}),1.0]])]});
            var Q3;
            Q3=makeQuery(id+"F15.imprint","IMPRINT",FACE,{"disambiguationData":[TD([[makeQuery(id+"F15.imprint","IMPRINT",EDGE,{"derivedFrom":sQuery(id+"F15.wireOp",EDGE,"E45")}),1.0]])]});
            var Q4;
            Q4=makeQuery(id+"F15.imprint","IMPRINT",FACE,{"disambiguationData":[TD([[makeQuery(id+"F15.imprint","IMPRINT",EDGE,{"derivedFrom":sQuery(id+"F15.wireOp",EDGE,"E39")}),1.0]])]});
            var Q5;
            Q5=makeQuery(id+"F15.imprint","IMPRINT",FACE,{"disambiguationData":[TD([[makeQuery(id+"F15.imprint","IMPRINT",EDGE,{"derivedFrom":sQuery(id+"F15.wireOp",EDGE,"E46")}),1.0]])]});
            var Q6;
            Q6=makeQuery(id+"F15.imprint","IMPRINT",FACE,{"disambiguationData":[TD([[makeQuery(id+"F15.imprint","IMPRINT",EDGE,{"derivedFrom":sQuery(id+"F15.wireOp",EDGE,"E41")}),1.0]])]});
            var Q7;
            Q7=makeQuery(id+"F15.imprint","IMPRINT",FACE,{"disambiguationData":[TD([[makeQuery(id+"F15.imprint","IMPRINT",EDGE,{"derivedFrom":sQuery(id+"F15.wireOp",EDGE,"E42")}),1.0]])]});
            var Q8;
            Q8=makeQuery(id+"F15.imprint","IMPRINT",FACE,{"disambiguationData":[TD([[makeQuery(id+"F15.imprint","IMPRINT",EDGE,{"derivedFrom":sQuery(id+"F15.wireOp",EDGE,"E48")}),1.0]])]});
            var Q9;
            Q9=makeQuery(id+"F15.imprint","IMPRINT",FACE,{"disambiguationData":[TD([[makeQuery(id+"F15.imprint","IMPRINT",EDGE,{"derivedFrom":sQuery(id+"F15.wireOp",EDGE,"E47")}),1.0]])]});
            extrude(context, id + "F16", {"entities" : qUnion([Q0, Q1, Q2, Q3, Q4, Q5, Q6, Q7, Q8, Q9]), "operationType" : NewBodyOperationType.REMOVE, "endBound" : BoundingType.THROUGH_ALL, "oppositeDirection" : true, "depth" : 25.4 * mm});
        }
    });
